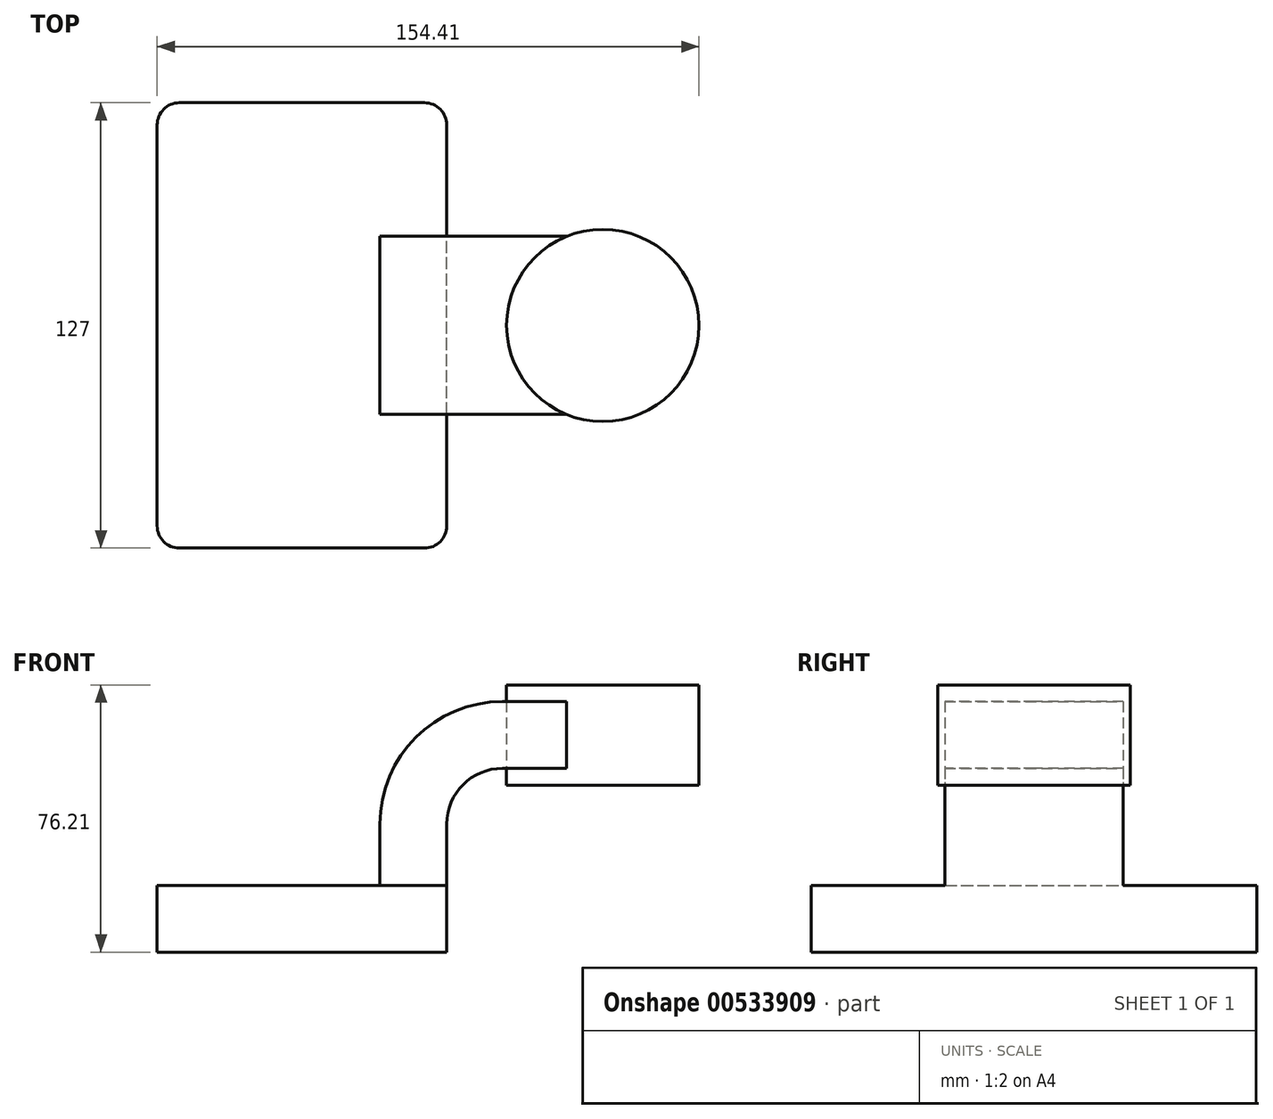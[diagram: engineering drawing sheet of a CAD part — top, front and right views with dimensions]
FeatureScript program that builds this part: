
annotation { "Feature Type Name" : "Feature", "Feature Type Description" : "" }
export const myFeature = defineFeature(function(context is Context, id is Id, definition is map)
    precondition{}
    {
        {
            var Q0;
            Q0=qCreatedBy(makeId("Front.planeOp"),FACE);
            var sketch = newSketch(context, id + "F0", { "sketchPlane" : qUnion([Q0])});
            skLineSegment(sketch, "E0.bottom", {"start": v(-41.28, 9.52) * mm, "end": v(41.28, 9.53) * mm});
            skLineSegment(sketch, "E0.top", {"start": v(-41.28, -9.53) * mm, "end": v(41.28, -9.53) * mm});
            skLineSegment(sketch, "E0.left", {"start": v(-41.28, 9.52) * mm, "end": v(-41.28, -9.53) * mm});
            skLineSegment(sketch, "E0.right", {"start": v(41.28, 9.53) * mm, "end": v(41.28, -9.52) * mm});
            skPoint(sketch, "E0.middle", {"position": v(0, 0) * mm});
            skLineSegment(sketch, "E1", {"start": v(41.27, 9.53) * mm, "end": v(41.27, 27) * mm});
            skLineSegment(sketch, "E2.bottom", {"start": v(113.14, 38.1) * mm, "end": v(62.34, 38.1) * mm});
            skLineSegment(sketch, "E2.top", {"start": v(113.14, 66.68) * mm, "end": v(62.34, 66.68) * mm});
            skLineSegment(sketch, "E2.left", {"start": v(113.14, 38.1) * mm, "end": v(113.14, 66.68) * mm});
            skLineSegment(sketch, "E2.right", {"start": v(62.34, 38.1) * mm, "end": v(62.34, 66.68) * mm});
            skPoint(sketch, "E2.middle", {"position": v(87.74, 52.39) * mm});
            skArc(sketch, "E3", {"start": v(41.27, 27) * mm, "mid": v(45.92, 38.23) * mm, "end": v(57.15, 42.88) * mm});
            skLineSegment(sketch, "E4", {"start": v(57.15, 42.88) * mm, "end": v(85.72, 42.88) * mm});
            skLineSegment(sketch, "E5.0", {"start": v(57.15, 61.93) * mm, "end": v(85.72, 61.93) * mm});
            skArc(sketch, "E5.1", {"start": v(22.22, 27) * mm, "mid": v(32.45, 51.7) * mm, "end": v(57.15, 61.93) * mm});
            skLineSegment(sketch, "E5.2", {"start": v(22.22, 9.53) * mm, "end": v(22.22, 27) * mm});
            skLineSegment(sketch, "E6", {"start": v(85.72, 38.1) * mm, "end": v(85.72, 66.68) * mm});
            skFitSpline(sketch, "E7", {"points": [v(-41.28, 9.52) * mm, v(57.15, 61.93) * mm], "startDerivative": vector(-1.38, 84.73) * mm, "endDerivative": vector(156.04, -0.12) * mm});
            skSolve(sketch);
        }
        {
            var Q0;
            Q0=makeQuery(id+"F0.imprint","IMPRINT",FACE,{"disambiguationData":[TD([[makeQuery(id+"F0.imprint","IMPRINT",EDGE,{"derivedFrom":sQuery(id+"F0.wireOp",EDGE,"E0.top")}),1.0]])]});
            extrude(context, id + "F1", {"entities" : qUnion([Q0]), "endBound" : BoundingType.SYMMETRIC, "depth" : 127 * mm, "offsetDistance" : 25.4 * mm});
        }
        {
            var Q0;
            {var subQ6=sQuery(id+"F0.wireOp",EDGE,"E1");Q0=makeQuery(id+"F0.imprint","IMPRINT",FACE,{"disambiguationData":[TD([[makeQuery(id+"F0.imprint","IMPRINT",EDGE,{"derivedFrom":subQ6}),1.0]])]});}
            var Q1;
            {var subQ0=sQuery(id+"F0.wireOp",EDGE,"E4");var subQ1=sQuery(id+"F0.wireOp",EDGE,"E2.right");var subQ2=makeQuery(id+"F0.imprint","INTERSECT",VERTEX,{"derivedFrom":[subQ1,subQ0]});Q1=makeQuery(id+"F0.imprint","IMPRINT",FACE,{"disambiguationData":[TD([[makeQuery(id+"F0.imprint","IMPRINT",EDGE,{"disambiguationData":[TD([[subQ2,-1.0]])],"derivedFrom":subQ1}),-1.0]])]});}
            extrude(context, id + "F2", {"entities" : qUnion([Q0, Q1]), "operationType" : NewBodyOperationType.ADD, "endBound" : BoundingType.SYMMETRIC, "depth" : 50.8 * mm, "offsetDistance" : 25.4 * mm});
        }
        {
            var Q0;
            Q0=makeQuery(id+"F0.imprint","IMPRINT",FACE,{"disambiguationData":[TD([[makeQuery(id+"F0.imprint","IMPRINT",EDGE,{"derivedFrom":sQuery(id+"F0.wireOp",EDGE,"E5.1")}),1.0]])]});
            extrude(context, id + "F3", {"entities" : qUnion([Q0]), "operationType" : NewBodyOperationType.ADD, "endBound" : BoundingType.SYMMETRIC, "depth" : 15.88 * mm, "offsetDistance" : 25.4 * mm});
        }
        {
            var Q0;
            {var subQ0=sQuery(id+"F0.wireOp",EDGE,"E2.left");Q0=makeQuery(id+"F0.imprint","IMPRINT",FACE,{"disambiguationData":[TD([[makeQuery(id+"F0.imprint","IMPRINT",EDGE,{"derivedFrom":subQ0}),1.0]])]});}
            var Q1;
            Q1=sQuery(id+"F0.wireOp",EDGE,"E6");
            revolve(context, id + "F4", {"entities" : qUnion([Q0]), "axis" : qUnion([Q1]), "revolveType" : RevolveType.FULL});
        }
        {
            var Q0;
            Q0=makeQuery(id+"F1.opExtrude","CAP_EDGE",EDGE,{"disambiguationData":[OSD([sQuery(id+"F0.wireOp",EDGE,"E0.right")])],"isStart":false});
            var Q1;
            Q1=makeQuery(id+"F1.opExtrude","CAP_EDGE",EDGE,{"disambiguationData":[OSD([sQuery(id+"F0.wireOp",EDGE,"E0.right")])],"isStart":true});
            var Q2;
            Q2=makeQuery(id+"F1.opExtrude","CAP_EDGE",EDGE,{"disambiguationData":[OSD([sQuery(id+"F0.wireOp",EDGE,"E0.left")])],"isStart":true});
            var Q3;
            Q3=makeQuery(id+"F1.opExtrude","CAP_EDGE",EDGE,{"disambiguationData":[OSD([sQuery(id+"F0.wireOp",EDGE,"E0.left")])],"isStart":false});
            fillet(context, id + "F5", {"entities" : qUnion([Q0, Q1, Q2, Q3]), "radius" : 6.35 * mm, "tangentPropagation" : true, "allowEdgeOverflow" : false});
        }
    });
